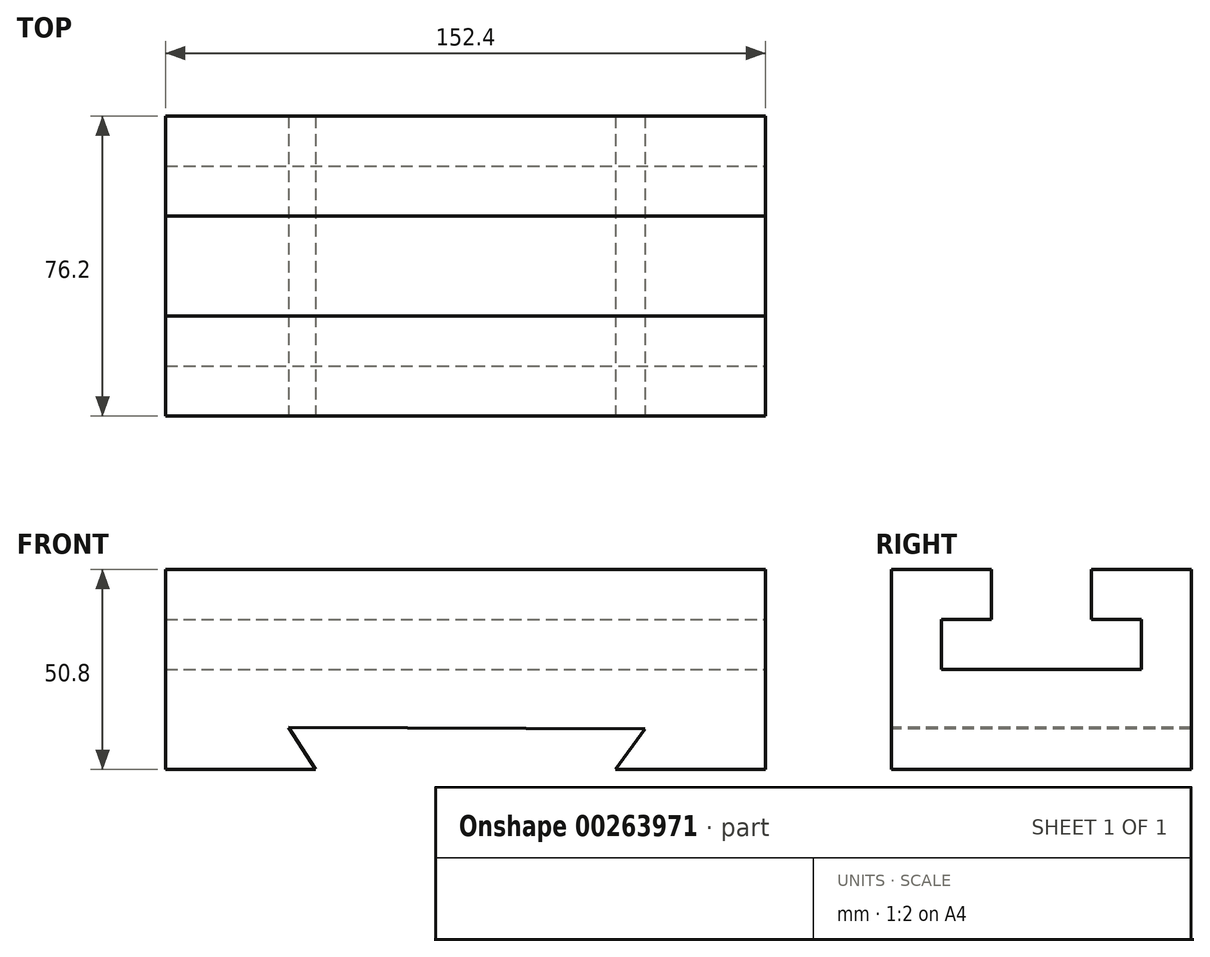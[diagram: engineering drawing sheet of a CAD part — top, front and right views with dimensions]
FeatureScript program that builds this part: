
annotation { "Feature Type Name" : "Feature", "Feature Type Description" : "" }
export const myFeature = defineFeature(function(context is Context, id is Id, definition is map)
    precondition{}
    {
        {
            var Q0;
            Q0=qCreatedBy(makeId("Right.planeOp"),FACE);
            var sketch = newSketch(context, id + "F0", { "sketchPlane" : qUnion([Q0])});
            skLineSegment(sketch, "E0", {"start": v(-76.2, -75.79) * mm, "end": v(0, -75.79) * mm});
            skLineSegment(sketch, "E1", {"start": v(0, -75.79) * mm, "end": v(0, -24.99) * mm});
            skLineSegment(sketch, "E2", {"start": v(0, -24.99) * mm, "end": v(-25.4, -24.99) * mm});
            skLineSegment(sketch, "E3", {"start": v(-76.2, -75.79) * mm, "end": v(-76.2, -24.99) * mm});
            skLineSegment(sketch, "E4", {"start": v(-76.2, -24.99) * mm, "end": v(-50.8, -24.99) * mm});
            skLineSegment(sketch, "E5", {"start": v(-50.8, -24.99) * mm, "end": v(-50.8, -37.69) * mm});
            skLineSegment(sketch, "E6", {"start": v(-50.8, -37.69) * mm, "end": v(-63.5, -37.69) * mm});
            skLineSegment(sketch, "E7", {"start": v(-63.5, -37.69) * mm, "end": v(-63.5, -50.39) * mm});
            skLineSegment(sketch, "E8", {"start": v(-63.5, -50.39) * mm, "end": v(-12.7, -50.39) * mm});
            skLineSegment(sketch, "E9", {"start": v(-12.7, -50.39) * mm, "end": v(-12.7, -37.69) * mm});
            skLineSegment(sketch, "E10", {"start": v(-12.7, -37.69) * mm, "end": v(-25.4, -37.69) * mm});
            skLineSegment(sketch, "E11", {"start": v(-25.4, -37.69) * mm, "end": v(-25.4, -24.99) * mm});
            skSolve(sketch);
        }
        {
            var Q0;
            Q0=makeQuery(id+"F0.imprint","IMPRINT",FACE,{"disambiguationData":[TD([[makeQuery(id+"F0.imprint","IMPRINT",EDGE,{"derivedFrom":sQuery(id+"F0.wireOp",EDGE,"E0")}),1.0]])]});
            extrude(context, id + "F1", {"entities" : qUnion([Q0]), "oppositeDirection" : true, "depth" : 152.4 * mm});
        }
        {
            var Q0;
            Q0=makeQuery(id+"F1.opExtrude","SWEPT_FACE",FACE,{"disambiguationData":[OSD([sQuery(id+"F0.wireOp",EDGE,"E3")])]});
            var sketch = newSketch(context, id + "F2", { "sketchPlane" : qUnion([Q0])});
            skLineSegment(sketch, "E12", {"start": v(-152.4, -75.79) * mm, "end": v(-114.3, -75.79) * mm});
            skLineSegment(sketch, "E13", {"start": v(0, -75.79) * mm, "end": v(-38.1, -75.79) * mm});
            skLineSegment(sketch, "E14", {"start": v(-114.3, -75.79) * mm, "end": v(-121.21, -65.13) * mm});
            skLineSegment(sketch, "E15", {"start": v(-38.1, -75.79) * mm, "end": v(-30.63, -65.52) * mm});
            skLineSegment(sketch, "E16", {"start": v(-30.63, -65.52) * mm, "end": v(-121.21, -65.13) * mm});
            skSolve(sketch);
        }
        {
            var Q0;
            {var subQ0=sQuery(id+"F2.wireOp",EDGE,"E14");Q0=makeQuery(id+"F2.imprint","IMPRINT",FACE,{"disambiguationData":[TD([[makeQuery(id+"F2.imprint","IMPRINT",EDGE,{"derivedFrom":subQ0}),-1.0]])]});}
            extrude(context, id + "F3", {"entities" : qUnion([Q0]), "operationType" : NewBodyOperationType.REMOVE, "endBound" : BoundingType.UP_TO_NEXT, "oppositeDirection" : true, "depth" : 25.4 * mm});
        }
    });
